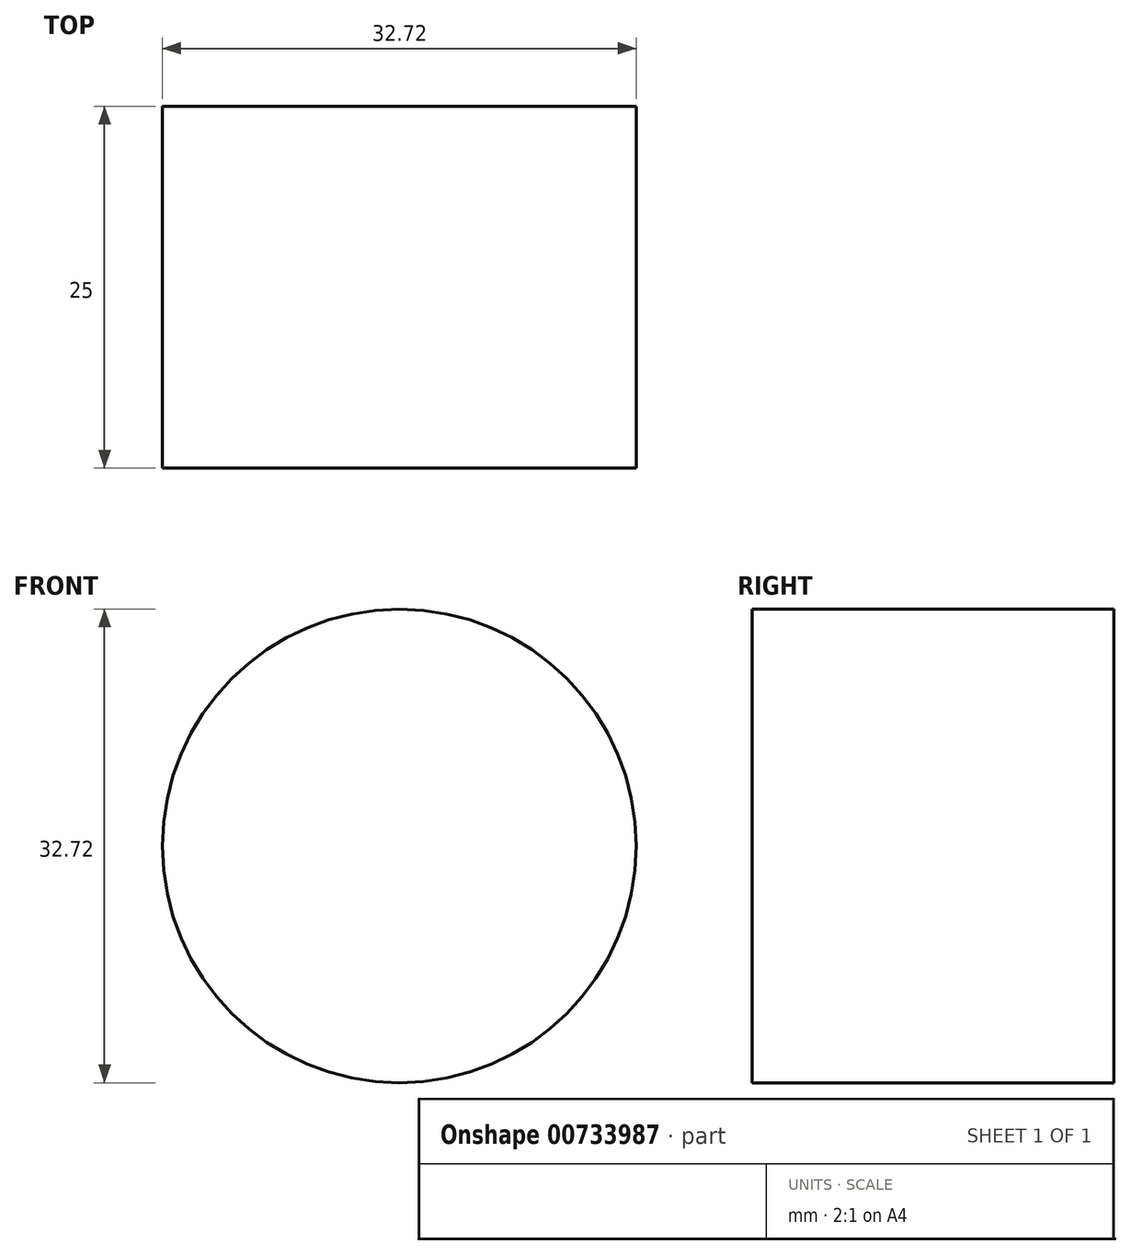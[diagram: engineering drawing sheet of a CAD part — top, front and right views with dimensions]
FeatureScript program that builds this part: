
annotation { "Feature Type Name" : "Feature", "Feature Type Description" : "" }
export const myFeature = defineFeature(function(context is Context, id is Id, definition is map)
    precondition{}
    {
        {
            var Q0;
            Q0=qCreatedBy(makeId("Front.planeOp"),FACE);
            var sketch = newSketch(context, id + "F0", { "sketchPlane" : qUnion([Q0])});
            skCircle(sketch, "E0", {"center": v(-76.91, 57.95) * mm, "radius": 16.36 * mm});
            skSolve(sketch);
        }
        {
            var Q0;
            Q0 = qSketchRegion(id + "F0", true);
            extrude(context, id + "F1", {"entities" : qUnion([Q0]), "depth" : 25 * mm, "offsetDistance" : 25 * mm});
        }
    });
